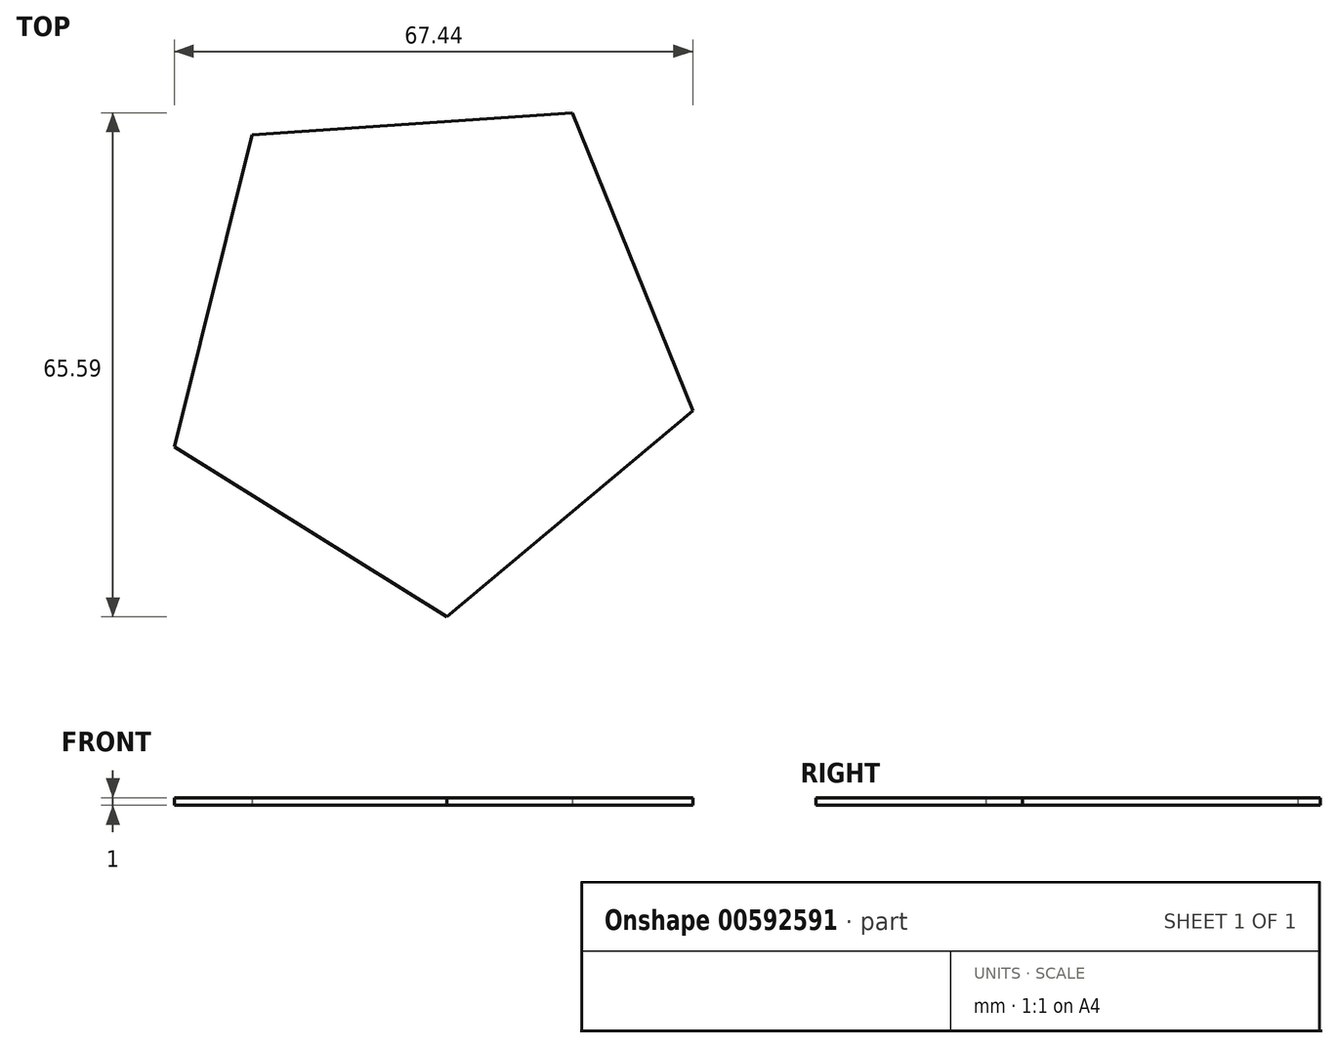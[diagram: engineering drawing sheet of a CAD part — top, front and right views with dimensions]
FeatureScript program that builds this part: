
annotation { "Feature Type Name" : "Feature", "Feature Type Description" : "" }
export const myFeature = defineFeature(function(context is Context, id is Id, definition is map)
    precondition{}
    {
        {
            var Q0;
            Q0=qCreatedBy(makeId("Top.planeOp"),FACE);
            var sketch = newSketch(context, id + "F0", { "sketchPlane" : qUnion([Q0])});
            skLineSegment(sketch, "E0.0", {"start": v(-23.56, 23.54) * mm, "end": v(19.92, 26.69) * mm});
            skLineSegment(sketch, "E0.1", {"start": v(19.92, 26.69) * mm, "end": v(36.35, -13.7) * mm});
            skLineSegment(sketch, "E0.2", {"start": v(36.35, -13.7) * mm, "end": v(3.02, -41.8) * mm});
            skLineSegment(sketch, "E0.3", {"start": v(3.02, -41.8) * mm, "end": v(-34, -18.79) * mm});
            skLineSegment(sketch, "E0.4", {"start": v(-34, -18.79) * mm, "end": v(-23.56, 23.54) * mm});
            skPoint(sketch, "E0.0.midPoint", {"position": v(-1.82, 25.11) * mm});
            skLineSegment(sketch, "E1.0", {"start": v(-22.75, 22.6) * mm, "end": v(19.28, 25.62) * mm});
            skLineSegment(sketch, "E1.1", {"start": v(19.28, 25.62) * mm, "end": v(35.14, -13.42) * mm});
            skLineSegment(sketch, "E1.2", {"start": v(35.14, -13.42) * mm, "end": v(2.91, -40.56) * mm});
            skLineSegment(sketch, "E1.3", {"start": v(2.91, -40.56) * mm, "end": v(-32.87, -18.3) * mm});
            skLineSegment(sketch, "E1.4", {"start": v(-32.87, -18.3) * mm, "end": v(-22.75, 22.6) * mm});
            skPoint(sketch, "E1.0.midPoint", {"position": v(-1.73, 24.11) * mm});
            skLineSegment(sketch, "E2.0", {"start": v(-21.95, 21.66) * mm, "end": v(18.63, 24.57) * mm});
            skLineSegment(sketch, "E2.1", {"start": v(18.63, 24.57) * mm, "end": v(33.94, -13.12) * mm});
            skLineSegment(sketch, "E2.2", {"start": v(33.94, -13.12) * mm, "end": v(2.82, -39.33) * mm});
            skLineSegment(sketch, "E2.3", {"start": v(2.82, -39.33) * mm, "end": v(-31.72, -17.84) * mm});
            skLineSegment(sketch, "E2.4", {"start": v(-31.72, -17.84) * mm, "end": v(-21.95, 21.66) * mm});
            skPoint(sketch, "E2.0.midPoint", {"position": v(-1.66, 23.12) * mm});
            skLineSegment(sketch, "E3.0", {"start": v(-22.5, 22.41) * mm, "end": v(19.18, 25.33) * mm});
            skLineSegment(sketch, "E3.1", {"start": v(19.18, 25.33) * mm, "end": v(34.83, -13.4) * mm});
            skLineSegment(sketch, "E3.2", {"start": v(34.83, -13.4) * mm, "end": v(2.82, -40.26) * mm});
            skLineSegment(sketch, "E3.3", {"start": v(2.82, -40.26) * mm, "end": v(-32.6, -18.12) * mm});
            skLineSegment(sketch, "E3.4", {"start": v(-32.6, -18.12) * mm, "end": v(-22.5, 22.41) * mm});
            skPoint(sketch, "E3.0.midPoint", {"position": v(-1.66, 23.87) * mm});
            skSolve(sketch);
        }
        {
            var Q0;
            Q0=makeQuery(id+"F0.imprint","IMPRINT",FACE,{"disambiguationData":[TD([[makeQuery(id+"F0.imprint","IMPRINT",EDGE,{"derivedFrom":sQuery(id+"F0.wireOp",EDGE,"E2.0")}),-1.0]])]});
            var Q1;
            Q1=makeQuery(id+"F0.imprint","IMPRINT",FACE,{"disambiguationData":[TD([[makeQuery(id+"F0.imprint","IMPRINT",EDGE,{"derivedFrom":sQuery(id+"F0.wireOp",EDGE,"E2.0")}),1.0]])]});
            extrude(context, id + "F1", {"entities" : qUnion([Q0, Q1]), "depth" : 1 * mm, "offsetDistance" : 25 * mm});
        }
    });
